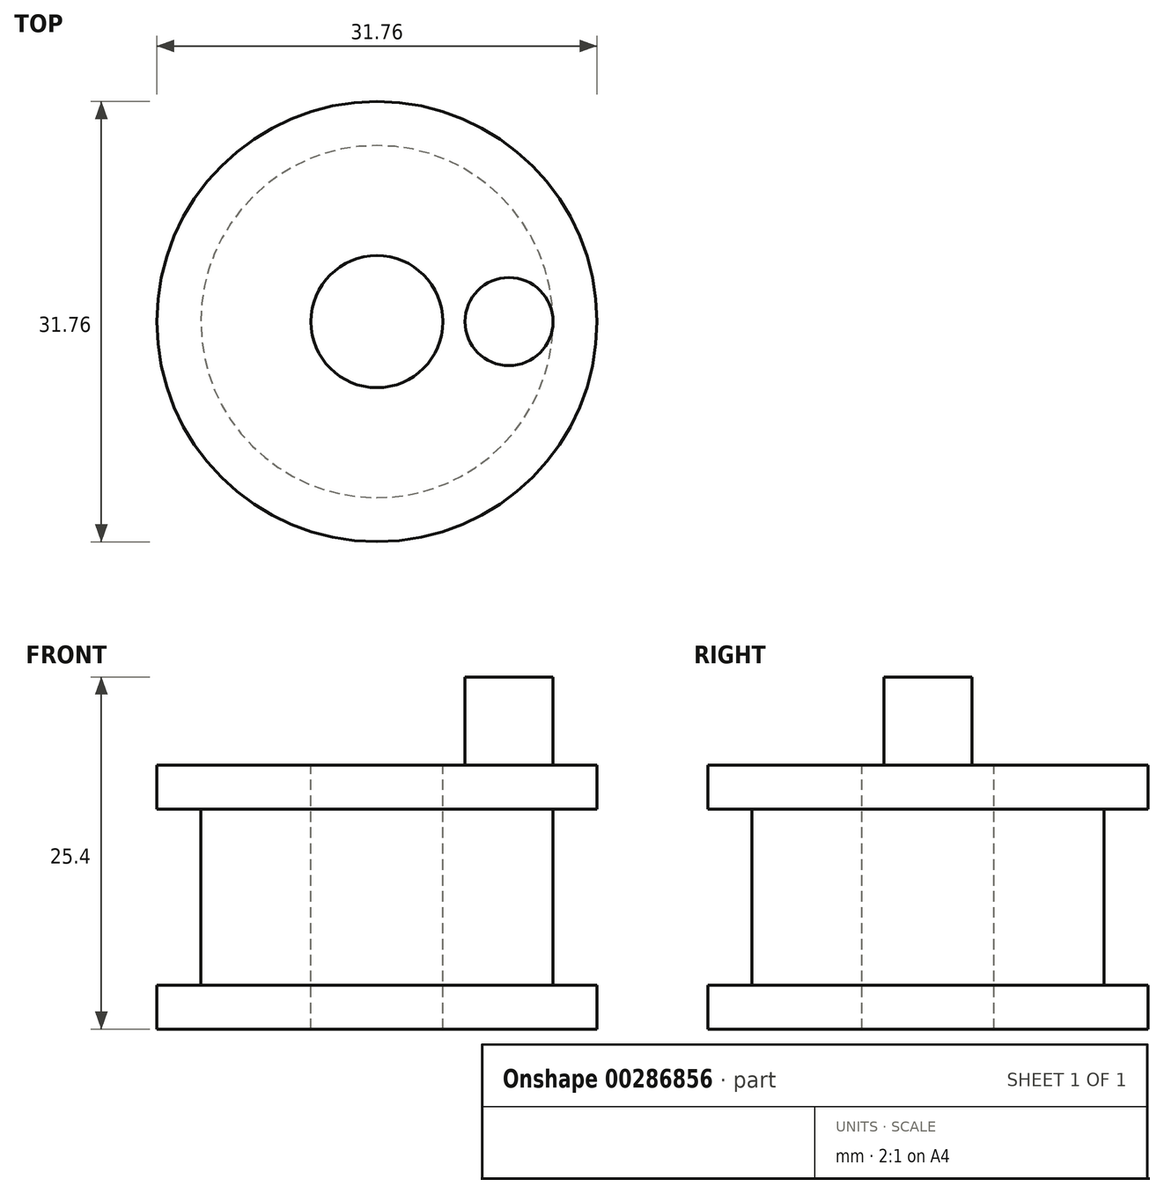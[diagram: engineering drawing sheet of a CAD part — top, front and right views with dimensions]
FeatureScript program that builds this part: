
annotation { "Feature Type Name" : "Feature", "Feature Type Description" : "" }
export const myFeature = defineFeature(function(context is Context, id is Id, definition is map)
    precondition{}
    {
        {
            var Q0;
            Q0=qCreatedBy(makeId("Front.planeOp"),FACE);
            var sketch = newSketch(context, id + "F0", { "sketchPlane" : qUnion([Q0])});
            skLineSegment(sketch, "E0.bottom", {"start": v(0, -1.52) * mm, "end": v(-15.87, -1.52) * mm});
            skLineSegment(sketch, "E0.top", {"start": v(0, -20.57) * mm, "end": v(-15.87, -20.57) * mm});
            skLineSegment(sketch, "E0.left", {"start": v(0, -1.52) * mm, "end": v(0, -20.57) * mm});
            skLineSegment(sketch, "E0.right", {"start": v(-15.87, -1.52) * mm, "end": v(-15.87, -4.7) * mm});
            skLineSegment(sketch, "E1", {"start": v(-15.88, -4.7) * mm, "end": v(-12.7, -4.7) * mm});
            skLineSegment(sketch, "E2", {"start": v(0, -4.7) * mm, "end": v(0, -17.4) * mm});
            skLineSegment(sketch, "E3", {"start": v(-12.7, -17.4) * mm, "end": v(-15.87, -17.4) * mm});
            skLineSegment(sketch, "E4", {"start": v(-12.7, -4.7) * mm, "end": v(-12.7, -17.4) * mm});
            skLineSegment(sketch, "E5.trimOffspring", {"start": v(-15.87, -17.4) * mm, "end": v(-15.87, -20.57) * mm});
            skSolve(sketch);
        }
        {
            var Q0;
            {var subQ3=sQuery(id+"F0.wireOp",EDGE,"E0.bottom");Q0=makeQuery(id+"F0.imprint","IMPRINT",FACE,{"disambiguationData":[TD([[makeQuery(id+"F0.imprint","IMPRINT",EDGE,{"derivedFrom":subQ3}),1.0]])]});}
            var Q1;
            Q1=sQuery(id+"F0.wireOp",EDGE,"E2");
            revolve(context, id + "F1", {"entities" : qUnion([Q0]), "axis" : qUnion([Q1]), "revolveType" : RevolveType.FULL});
        }
        {
            var Q0;
            Q0=makeQuery(id+"F1.opRevolve","SWEPT_FACE",FACE,{"disambiguationData":[OSD([sQuery(id+"F0.wireOp",EDGE,"E0.bottom")])]});
            var sketch = newSketch(context, id + "F2", { "sketchPlane" : qUnion([Q0])});
            skCircle(sketch, "E6", {"center": v(0, 0) * mm, "radius": 4.76 * mm});
            skCircle(sketch, "E7", {"center": v(9.53, 0) * mm, "radius": 3.18 * mm});
            skSolve(sketch);
        }
        {
            var Q0;
            Q0=sQuery(id+"F2.wireOp",VERTEX,"E6.center");
            var Q1;
            Q1=makeQuery(id+"F1.opRevolve","SWEPT_BODY",BODY,{"disambiguationData":[OSD([sQuery(id+"F0.wireOp",EDGE,"E0.bottom"),sQuery(id+"F0.wireOp",EDGE,"E0.top"),sQuery(id+"F0.wireOp",EDGE,"E0.left"),sQuery(id+"F0.wireOp",EDGE,"E0.right"),sQuery(id+"F0.wireOp",EDGE,"E1"),sQuery(id+"F0.wireOp",EDGE,"E2"),sQuery(id+"F0.wireOp",EDGE,"E3"),sQuery(id+"F0.wireOp",EDGE,"E4"),sQuery(id+"F0.wireOp",EDGE,"E5.trimOffspring")])]});
            hole(context, id + "F3", {"style" : HoleStyle.SIMPLE, "endStyle" : HoleEndStyle.THROUGH, "holeDiameter" : 9.52 * mm, "tappedDepth" : 12.7 * mm, "tapClearance" : 3, "locations" : qUnion([Q0]), "scope" : qUnion([Q1])});
        }
        {
            var Q0;
            Q0=makeQuery(id+"F1.opRevolve","SWEPT_FACE",FACE,{"disambiguationData":[OSD([sQuery(id+"F0.wireOp",EDGE,"E0.bottom")])]});
            var sketch = newSketch(context, id + "F4", { "sketchPlane" : qUnion([Q0])});
            skCircle(sketch, "E8", {"center": v(9.53, 0) * mm, "radius": 3.18 * mm});
            skSolve(sketch);
        }
        {
            var Q0;
            Q0=makeQuery(id+"F4.imprint","IMPRINT",FACE,{"disambiguationData":[TD([[makeQuery(id+"F4.imprint","IMPRINT",EDGE,{"derivedFrom":sQuery(id+"F4.wireOp",EDGE,"E8")}),1.0]])]});
            extrude(context, id + "F5", {"entities" : qUnion([Q0]), "operationType" : NewBodyOperationType.ADD, "depth" : 6.35 * mm});
        }
    });
